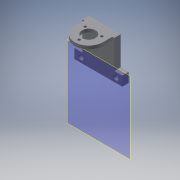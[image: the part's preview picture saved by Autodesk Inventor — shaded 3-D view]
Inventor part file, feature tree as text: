
AUTODESK INVENTOR PART (.ipt)
format: ipt  version: 2016 (Build 200138000, 138)  size: 147,968 bytes
history: native  units: mm
features: extrude x2, sketch x2, reference x2, plane x1
ambient origin geometry x8: Origin, YZ Plane, XZ Plane, XY Plane, X Axis, Y Axis, Z Axis, Center Point
bodies: Solid1 (feature_tree)
feature tree (7):
  plane  "Work Plane1"
  extrude  "Extrusion1"  Depth=15.0mm
  extrude  "Extrusion2"  Depth=50.0mm
  sketch  "Sketch1"  dims[d0=75.0mm d1=15.0mm]
  sketch  "Sketch2"  dims[d2=40.0mm d3=50.0mm d4=10.0mm d5=0.0mm d6=22.0mm d7=21.0mm d8=30.0mm d9=4.0mm d10=120.0deg d11=120.0deg d12=5.0mm d13=0.0mm d14=8.0mm]
  reference  "Reference2"
  reference  "Reference3"
